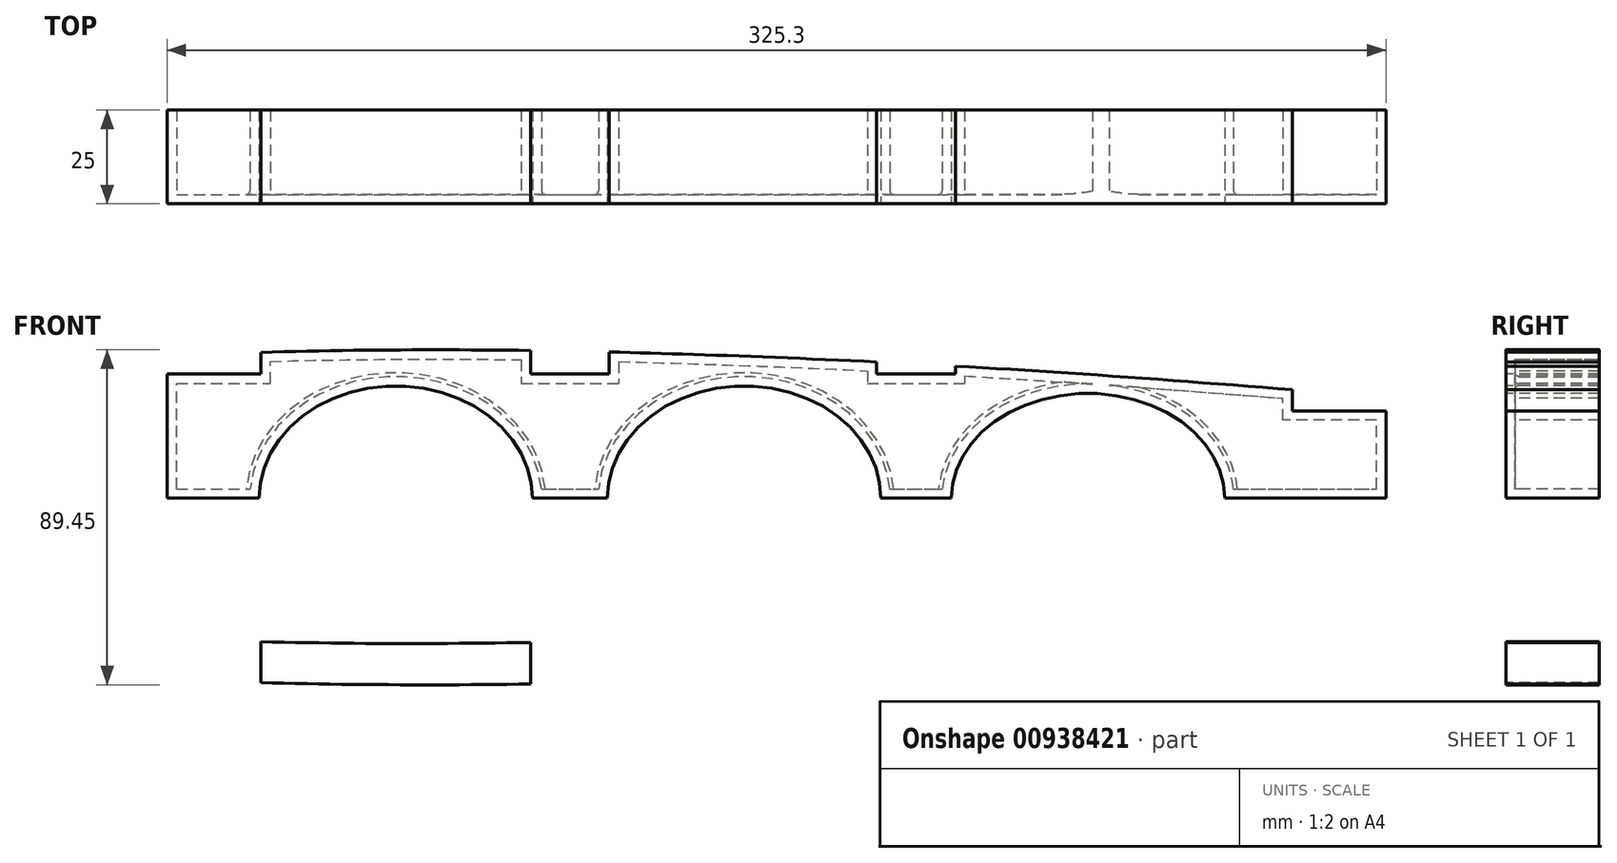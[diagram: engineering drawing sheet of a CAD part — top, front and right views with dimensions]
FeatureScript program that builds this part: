
annotation { "Feature Type Name" : "Feature", "Feature Type Description" : "" }
export const myFeature = defineFeature(function(context is Context, id is Id, definition is map)
    precondition{}
    {
        {
            var Q0;
            Q0=qCreatedBy(makeId("Front.planeOp"),FACE);
            var sketch = newSketch(context, id + "F0", { "sketchPlane" : qUnion([Q0])});
            skLineSegment(sketch, "E0", {"start": v(0, 0) * mm, "end": v(830, 0) * mm});
            skLineSegment(sketch, "E1", {"start": v(23.53, 0) * mm, "end": v(23.53, 22.98) * mm, "construction": true});
            skLineSegment(sketch, "E2", {"start": v(30.64, 0) * mm, "end": v(30.64, 25.86) * mm, "construction": true});
            skLineSegment(sketch, "E3", {"start": v(38.65, 0) * mm, "end": v(38.65, 28.62) * mm, "construction": true});
            skLineSegment(sketch, "E4", {"start": v(47.54, 0) * mm, "end": v(47.54, 31.24) * mm, "construction": true});
            skLineSegment(sketch, "E5", {"start": v(57.28, 0) * mm, "end": v(57.28, 33.72) * mm, "construction": true});
            skLineSegment(sketch, "E6", {"start": v(67.86, 0) * mm, "end": v(67.86, 36.05) * mm, "construction": true});
            skLineSegment(sketch, "E7", {"start": v(79.26, 0) * mm, "end": v(79.26, 38.22) * mm, "construction": true});
            skLineSegment(sketch, "E8", {"start": v(91.44, 0) * mm, "end": v(91.44, 40.22) * mm, "construction": true});
            skLineSegment(sketch, "E9", {"start": v(104.37, 0) * mm, "end": v(104.37, 42.04) * mm, "construction": true});
            skLineSegment(sketch, "E10", {"start": v(118.03, 0) * mm, "end": v(118.03, 43.68) * mm, "construction": true});
            skLineSegment(sketch, "E11", {"start": v(132.38, 0) * mm, "end": v(132.38, 45.13) * mm, "construction": true});
            skLineSegment(sketch, "E12", {"start": v(147.4, 0) * mm, "end": v(147.4, 46.38) * mm, "construction": true});
            skLineSegment(sketch, "E13", {"start": v(163.03, 0) * mm, "end": v(163.03, 47.45) * mm, "construction": true});
            skLineSegment(sketch, "E14", {"start": v(179.25, 0) * mm, "end": v(179.25, 48.31) * mm, "construction": true});
            skLineSegment(sketch, "E15", {"start": v(196.03, 0) * mm, "end": v(196.03, 48.98) * mm, "construction": true});
            skLineSegment(sketch, "E16", {"start": v(213.32, 0) * mm, "end": v(213.32, 49.45) * mm, "construction": true});
            skLineSegment(sketch, "E17", {"start": v(231.08, 0) * mm, "end": v(231.08, 49.73) * mm, "construction": true});
            skLineSegment(sketch, "E18", {"start": v(249.26, 0) * mm, "end": v(249.26, 49.81) * mm, "construction": true});
            skLineSegment(sketch, "E19", {"start": v(267.84, 0) * mm, "end": v(267.84, 49.72) * mm, "construction": true});
            skLineSegment(sketch, "E20", {"start": v(0.48, 0) * mm, "end": v(0.48, 3.54) * mm, "construction": true});
            skLineSegment(sketch, "E21", {"start": v(1.94, 0) * mm, "end": v(1.94, 7) * mm, "construction": true});
            skLineSegment(sketch, "E22", {"start": v(4.35, 0) * mm, "end": v(4.35, 10.38) * mm, "construction": true});
            skLineSegment(sketch, "E23", {"start": v(7.73, 0) * mm, "end": v(7.73, 13.67) * mm, "construction": true});
            skLineSegment(sketch, "E24", {"start": v(12.06, 0) * mm, "end": v(12.06, 16.87) * mm, "construction": true});
            skLineSegment(sketch, "E25", {"start": v(17.33, 0) * mm, "end": v(17.33, 19.98) * mm, "construction": true});
            skLineSegment(sketch, "E26", {"start": v(286.76, 0) * mm, "end": v(286.76, 49.45) * mm, "construction": true});
            skLineSegment(sketch, "E27", {"start": v(305.98, 0) * mm, "end": v(305.98, 49) * mm, "construction": true});
            skLineSegment(sketch, "E28", {"start": v(325.45, 0) * mm, "end": v(325.45, 48.4) * mm, "construction": true});
            skLineSegment(sketch, "E29", {"start": v(345.13, 0) * mm, "end": v(345.13, 47.64) * mm, "construction": true});
            skLineSegment(sketch, "E30", {"start": v(364.98, 0) * mm, "end": v(364.98, 46.75) * mm, "construction": true});
            skLineSegment(sketch, "E31", {"start": v(384.94, 0) * mm, "end": v(384.94, 45.71) * mm, "construction": true});
            skLineSegment(sketch, "E32", {"start": v(404.97, 0) * mm, "end": v(404.97, 44.56) * mm, "construction": true});
            skLineSegment(sketch, "E33", {"start": v(425.03, 0) * mm, "end": v(425.03, 43.3) * mm, "construction": true});
            skLineSegment(sketch, "E34", {"start": v(445.06, 0) * mm, "end": v(445.06, 41.93) * mm, "construction": true});
            skLineSegment(sketch, "E35", {"start": v(465.02, 0) * mm, "end": v(465.02, 40.47) * mm, "construction": true});
            skLineSegment(sketch, "E36", {"start": v(484.87, 0) * mm, "end": v(484.87, 38.94) * mm, "construction": true});
            skLineSegment(sketch, "E37", {"start": v(504.55, 0) * mm, "end": v(504.55, 37.33) * mm, "construction": true});
            skLineSegment(sketch, "E38", {"start": v(524.02, 0) * mm, "end": v(524.02, 35.67) * mm, "construction": true});
            skLineSegment(sketch, "E39", {"start": v(543.24, 0) * mm, "end": v(543.24, 33.96) * mm, "construction": true});
            skLineSegment(sketch, "E40", {"start": v(562.16, 0) * mm, "end": v(562.16, 32.21) * mm, "construction": true});
            skLineSegment(sketch, "E41", {"start": v(580.74, 0) * mm, "end": v(580.74, 30.44) * mm, "construction": true});
            skLineSegment(sketch, "E42", {"start": v(598.92, 0) * mm, "end": v(598.92, 28.64) * mm, "construction": true});
            skLineSegment(sketch, "E43", {"start": v(633.97, 0) * mm, "end": v(633.97, 25.03) * mm, "construction": true});
            skLineSegment(sketch, "E44", {"start": v(616.68, 0) * mm, "end": v(616.68, 26.83) * mm, "construction": true});
            skLineSegment(sketch, "E45", {"start": v(650.75, 0) * mm, "end": v(650.75, 23.23) * mm, "construction": true});
            skLineSegment(sketch, "E46", {"start": v(666.97, 0) * mm, "end": v(666.97, 21.44) * mm, "construction": true});
            skLineSegment(sketch, "E47", {"start": v(682.6, 0) * mm, "end": v(682.6, 19.68) * mm, "construction": true});
            skLineSegment(sketch, "E48", {"start": v(697.62, 0) * mm, "end": v(697.62, 17.96) * mm, "construction": true});
            skLineSegment(sketch, "E49", {"start": v(711.97, 0) * mm, "end": v(711.97, 16.27) * mm, "construction": true});
            skLineSegment(sketch, "E50", {"start": v(725.63, 0) * mm, "end": v(725.63, 14.64) * mm, "construction": true});
            skLineSegment(sketch, "E51", {"start": v(738.56, 0) * mm, "end": v(738.56, 13.06) * mm, "construction": true});
            skLineSegment(sketch, "E52", {"start": v(750.74, 0) * mm, "end": v(750.74, 11.55) * mm, "construction": true});
            skLineSegment(sketch, "E53", {"start": v(762.14, 0) * mm, "end": v(762.14, 10.11) * mm, "construction": true});
            skLineSegment(sketch, "E54", {"start": v(791.35, 0) * mm, "end": v(791.35, 6.32) * mm, "construction": true});
            skLineSegment(sketch, "E55", {"start": v(799.36, 0) * mm, "end": v(799.36, 5.25) * mm, "construction": true});
            skLineSegment(sketch, "E56", {"start": v(806.47, 0) * mm, "end": v(806.47, 4.29) * mm, "construction": true});
            skLineSegment(sketch, "E57", {"start": v(782.46, 0) * mm, "end": v(782.46, 7.49) * mm, "construction": true});
            skLineSegment(sketch, "E58", {"start": v(812.67, 0) * mm, "end": v(812.67, 3.45) * mm, "construction": true});
            skLineSegment(sketch, "E59", {"start": v(817.94, 0) * mm, "end": v(817.94, 2.72) * mm, "construction": true});
            skLineSegment(sketch, "E60", {"start": v(822.27, 0) * mm, "end": v(822.27, 2.12) * mm, "construction": true});
            skLineSegment(sketch, "E61", {"start": v(825.65, 0) * mm, "end": v(825.65, 1.65) * mm, "construction": true});
            skLineSegment(sketch, "E62", {"start": v(828.06, 0) * mm, "end": v(828.06, 1.32) * mm, "construction": true});
            skLineSegment(sketch, "E63", {"start": v(772.72, 0) * mm, "end": v(772.72, 8.76) * mm, "construction": true});
            skLineSegment(sketch, "E64", {"start": v(829.52, 0) * mm, "end": v(829.52, 1.11) * mm, "construction": true});
            skLineSegment(sketch, "E65", {"start": v(830, 0) * mm, "end": v(830, 1.05) * mm});
            skFitSpline(sketch, "E66", {"points": [v(0, 0) * mm, v(0.48, 3.54) * mm, v(1.94, 7) * mm, v(4.35, 10.38) * mm, v(7.73, 13.67) * mm, v(12.06, 16.87) * mm, v(17.33, 19.98) * mm, v(23.53, 22.98) * mm, v(30.64, 25.86) * mm, v(38.65, 28.62) * mm, v(47.54, 31.24) * mm, v(57.28, 33.72) * mm, v(67.86, 36.05) * mm, v(79.26, 38.22) * mm, v(91.44, 40.22) * mm, v(104.37, 42.04) * mm, v(118.03, 43.68) * mm, v(132.38, 45.13) * mm, v(147.4, 46.39) * mm, v(163.03, 47.45) * mm, v(179.25, 48.31) * mm, v(196.03, 48.98) * mm, v(213.32, 49.45) * mm, v(231.08, 49.73) * mm, v(249.26, 49.81) * mm, v(267.84, 49.72) * mm, v(286.76, 49.45) * mm, v(305.98, 49) * mm, v(325.45, 48.4) * mm, v(345.13, 47.64) * mm, v(364.98, 46.75) * mm, v(384.94, 45.71) * mm, v(404.97, 44.56) * mm, v(425.03, 43.3) * mm, v(445.06, 41.93) * mm, v(465.02, 40.47) * mm, v(484.87, 38.94) * mm, v(504.55, 37.33) * mm, v(524.02, 35.67) * mm, v(543.24, 33.96) * mm, v(562.16, 32.21) * mm, v(580.74, 30.44) * mm, v(598.92, 28.64) * mm, v(616.68, 26.83) * mm, v(633.97, 25.03) * mm, v(650.75, 23.23) * mm, v(666.97, 21.44) * mm, v(682.6, 19.68) * mm, v(697.62, 17.96) * mm, v(711.97, 16.27) * mm, v(725.63, 14.64) * mm, v(738.56, 13.06) * mm, v(750.74, 11.55) * mm, v(762.14, 10.11) * mm, v(772.72, 8.76) * mm, v(782.46, 7.49) * mm, v(791.35, 6.32) * mm, v(799.36, 5.25) * mm, v(806.47, 4.29) * mm, v(812.67, 3.45) * mm, v(817.94, 2.72) * mm, v(822.27, 2.12) * mm, v(825.65, 1.65) * mm, v(828.06, 1.32) * mm, v(829.52, 1.11) * mm, v(830, 1.05) * mm], "startDerivative": vector(34.1, 427.03) * mm, "endDerivative": vector(137.1, -19.25) * mm});
            skFitSpline(sketch, "E67.MirrorCS", {"points": [v(0, 0) * mm, v(0.48, -3.54) * mm, v(1.94, -7) * mm, v(4.35, -10.38) * mm, v(7.73, -13.67) * mm, v(12.06, -16.87) * mm, v(17.33, -19.98) * mm, v(23.53, -22.98) * mm, v(30.64, -25.86) * mm, v(38.65, -28.62) * mm, v(47.54, -31.24) * mm, v(57.28, -33.72) * mm, v(67.86, -36.05) * mm, v(79.26, -38.22) * mm, v(91.44, -40.22) * mm, v(104.37, -42.04) * mm, v(118.03, -43.68) * mm, v(132.38, -45.13) * mm, v(147.4, -46.39) * mm, v(163.03, -47.45) * mm, v(179.25, -48.31) * mm, v(196.03, -48.98) * mm, v(213.32, -49.45) * mm, v(231.08, -49.73) * mm, v(249.26, -49.81) * mm, v(267.84, -49.72) * mm, v(286.76, -49.45) * mm, v(305.98, -49) * mm, v(325.45, -48.4) * mm, v(345.13, -47.64) * mm, v(364.98, -46.75) * mm, v(384.94, -45.71) * mm, v(404.97, -44.56) * mm, v(425.03, -43.3) * mm, v(445.06, -41.93) * mm, v(465.02, -40.47) * mm, v(484.87, -38.94) * mm, v(504.55, -37.33) * mm, v(524.02, -35.67) * mm, v(543.24, -33.96) * mm, v(562.16, -32.21) * mm, v(580.74, -30.44) * mm, v(598.92, -28.64) * mm, v(616.68, -26.83) * mm, v(633.97, -25.03) * mm, v(650.75, -23.23) * mm, v(666.97, -21.44) * mm, v(682.6, -19.68) * mm, v(697.62, -17.96) * mm, v(711.97, -16.27) * mm, v(725.63, -14.64) * mm, v(738.56, -13.06) * mm, v(750.74, -11.55) * mm, v(762.14, -10.11) * mm, v(772.72, -8.76) * mm, v(782.46, -7.49) * mm, v(791.35, -6.32) * mm, v(799.36, -5.25) * mm, v(806.47, -4.29) * mm, v(812.67, -3.45) * mm, v(817.94, -2.72) * mm, v(822.27, -2.12) * mm, v(825.65, -1.65) * mm, v(828.06, -1.32) * mm, v(829.52, -1.11) * mm, v(830, -1.05) * mm], "startDerivative": vector(34.1, -427.03) * mm, "endDerivative": vector(137.1, 19.25) * mm});
            skLineSegment(sketch, "E68.MirrorCS", {"start": v(830, 0) * mm, "end": v(830, -1.05) * mm});
            skLineSegment(sketch, "E69", {"start": v(163.03, 47.45) * mm, "end": v(163.03, -47.45) * mm});
            skLineSegment(sketch, "E70", {"start": v(204.25, -49.23) * mm, "end": v(204.25, -33.23) * mm});
            skLineSegment(sketch, "E71", {"start": v(204.25, -33.23) * mm, "end": v(179.25, -33.23) * mm});
            skLineSegment(sketch, "E72", {"start": v(179.25, -33.23) * mm, "end": v(179.25, 33.23) * mm});
            skLineSegment(sketch, "E73", {"start": v(179.25, 33.23) * mm, "end": v(204.25, 33.23) * mm});
            skLineSegment(sketch, "E74", {"start": v(204.25, 33.23) * mm, "end": v(204.25, 49.23) * mm});
            skLineSegment(sketch, "E75", {"start": v(524.02, 35.67) * mm, "end": v(524.02, -35.67) * mm});
            skLineSegment(sketch, "E76", {"start": v(479.55, -39.36) * mm, "end": v(479.55, -23.36) * mm});
            skLineSegment(sketch, "E77", {"start": v(479.55, -23.36) * mm, "end": v(504.55, -23.36) * mm});
            skLineSegment(sketch, "E78", {"start": v(504.55, -23.36) * mm, "end": v(504.55, 23.36) * mm});
            skLineSegment(sketch, "E79", {"start": v(504.55, 23.36) * mm, "end": v(479.55, 23.36) * mm});
            skLineSegment(sketch, "E80", {"start": v(479.55, 23.36) * mm, "end": v(479.55, 39.36) * mm});
            skEllipse(sketch, "E81", {"center": v(240.25, 0) * mm, "majorRadius": 36.5 * mm, "minorRadius": 30 * mm, "majorAxis": v(1, 0)});
            skEllipse(sketch, "E82.1.0.0", {"center": v(333.25, 0) * mm, "majorRadius": 36.5 * mm, "minorRadius": 30 * mm, "majorAxis": v(1, 0)});
            skLineSegment(sketch, "E82.direction1", {"start": v(240.25, 0) * mm, "end": v(333.25, 0) * mm, "construction": true});
            skEllipse(sketch, "E83", {"center": v(425.03, 0) * mm, "majorRadius": 28 * mm, "minorRadius": 36.5 * mm, "majorAxis": v(0, -1)});
            skFitSpline(sketch, "E84.0", {"points": [v(19.9, 0) * mm, v(19.93, 0.28) * mm, v(19.97, 0.77) * mm, v(20.03, 1.33) * mm, v(20.07, 1.63) * mm, v(20.1, 1.78) * mm, v(20.12, 1.85) * mm, v(20.12, 1.88) * mm, v(20.13, 1.92) * mm, v(20.16, 1.99) * mm, v(20.2, 2.1) * mm, v(20.28, 2.3) * mm, v(20.43, 2.58) * mm, v(20.63, 2.94) * mm, v(20.87, 3.32) * mm, v(21.13, 3.7) * mm, v(21.53, 4.23) * mm, v(22.12, 4.91) * mm, v(22.98, 5.8) * mm, v(24.01, 6.71) * mm, v(25.19, 7.65) * mm, v(26.5, 8.6) * mm, v(28.4, 9.86) * mm, v(31.06, 11.42) * mm, v(34.64, 13.25) * mm, v(38.55, 15) * mm, v(44.15, 17.24) * mm, v(51.77, 19.86) * mm, v(61.74, 22.7) * mm, v(72.4, 25.26) * mm, v(83.62, 27.56) * mm, v(95.37, 29.62) * mm, v(107.56, 31.45) * mm, v(124.36, 33.6) * mm, v(146.26, 35.8) * mm, v(173.73, 37.69) * mm, v(202.17, 38.91) * mm, v(231.43, 39.53) * mm, v(261.35, 39.6) * mm, v(291.8, 39.18) * mm, v(322.69, 38.31) * mm, v(364.28, 36.62) * mm, v(416.8, 33.63) * mm, v(479.93, 28.95) * mm, v(531.98, 24.38) * mm, v(572.9, 20.44) * mm, v(603.14, 17.37) * mm, v(632.79, 14.2) * mm, v(661.73, 10.99) * mm, v(689.84, 7.73) * mm, v(716.93, 4.47) * mm, v(738.52, 1.78) * mm, v(755.07, -0.33) * mm, v(767.08, -1.9) * mm, v(778.65, -3.43) * mm, v(789.72, -4.91) * mm, v(800.24, -6.35) * mm, v(810.11, -7.7) * mm, v(817.7, -8.77) * mm, v(823.32, -9.57) * mm, v(826.6, -10.03) * mm, v(829.07, -10.39) * mm, v(830.84, -10.64) * mm, v(832.51, -10.88) * mm, v(834.08, -11.1) * mm, v(835.26, -11.27) * mm, v(836.14, -11.4) * mm, v(836.78, -11.5) * mm, v(837.37, -11.58) * mm, v(837.78, -11.64) * mm, v(838.05, -11.68) * mm, v(838.28, -11.71) * mm, v(838.4, -11.73) * mm, v(838.5, -11.74) * mm]});
            skFitSpline(sketch, "E85.MirrorCS", {"points": [v(19.9, 0) * mm, v(19.93, -0.28) * mm, v(19.97, -0.77) * mm, v(20.03, -1.33) * mm, v(20.08, -1.63) * mm, v(20.1, -1.78) * mm, v(20.12, -1.85) * mm, v(20.13, -1.87) * mm, v(20.14, -1.92) * mm, v(20.16, -1.99) * mm, v(20.2, -2.1) * mm, v(20.29, -2.29) * mm, v(20.44, -2.58) * mm, v(20.64, -2.94) * mm, v(20.88, -3.31) * mm, v(21.15, -3.7) * mm, v(21.55, -4.22) * mm, v(22.13, -4.9) * mm, v(23, -5.78) * mm, v(24.04, -6.7) * mm, v(25.22, -7.63) * mm, v(26.52, -8.57) * mm, v(28.44, -9.83) * mm, v(31.1, -11.38) * mm, v(34.7, -13.2) * mm, v(38.6, -14.93) * mm, v(44.21, -17.15) * mm, v(51.85, -19.74) * mm, v(61.83, -22.54) * mm, v(72.49, -25.06) * mm, v(83.73, -27.32) * mm, v(95.48, -29.34) * mm, v(107.68, -31.12) * mm, v(124.49, -33.22) * mm, v(146.4, -35.32) * mm, v(173.87, -37.11) * mm, v(202.32, -38.23) * mm, v(231.57, -38.74) * mm, v(261.5, -38.7) * mm, v(291.95, -38.16) * mm, v(322.83, -37.18) * mm, v(364.42, -35.33) * mm, v(416.93, -32.14) * mm, v(480.03, -27.22) * mm, v(532.07, -22.46) * mm, v(572.98, -18.36) * mm, v(603.2, -15.18) * mm, v(632.84, -11.91) * mm, v(661.77, -8.58) * mm, v(689.86, -5.22) * mm, v(716.95, -1.86) * mm, v(738.52, 0.91) * mm, v(755.06, 3.1) * mm, v(767.06, 4.7) * mm, v(778.63, 6.27) * mm, v(789.7, 7.8) * mm, v(800.21, 9.27) * mm, v(810.08, 10.67) * mm, v(817.67, 11.77) * mm, v(823.28, 12.58) * mm, v(826.56, 13.06) * mm, v(829.03, 13.42) * mm, v(830.8, 13.68) * mm, v(832.47, 13.93) * mm, v(834.03, 14.16) * mm, v(835.21, 14.33) * mm, v(836.1, 14.46) * mm, v(836.73, 14.56) * mm, v(837.32, 14.64) * mm, v(837.73, 14.7) * mm, v(838, 14.75) * mm, v(838.23, 14.78) * mm, v(838.36, 14.8) * mm, v(838.45, 14.81) * mm]});
            skLineSegment(sketch, "E86", {"start": v(100.03, 30.3) * mm, "end": v(134.03, 30.3) * mm});
            skLineSegment(sketch, "E87", {"start": v(140.03, 24.3) * mm, "end": v(140.03, -24.26) * mm});
            skLineSegment(sketch, "E88", {"start": v(133.98, -30.26) * mm, "end": v(100.03, -29.99) * mm});
            skPoint(sketch, "E89.visualSharp", {"position": v(140.03, 30.3) * mm});
            skArc(sketch, "E89.filletArc", {"start": v(140.03, 24.3) * mm, "mid": v(138.27, 28.55) * mm, "end": v(134.03, 30.3) * mm});
            skPoint(sketch, "E90.visualSharp", {"position": v(140.03, -30.3) * mm});
            skArc(sketch, "E90.filletArc", {"start": v(133.98, -30.26) * mm, "mid": v(138.25, -28.52) * mm, "end": v(140.03, -24.26) * mm});
            skEllipse(sketch, "E91", {"center": v(569.02, 0) * mm, "majorRadius": 20 * mm, "minorRadius": 22.5 * mm, "majorAxis": v(0, -1)});
            skLineSegment(sketch, "E92.bottom", {"start": v(625.97, -12) * mm, "end": v(665.97, -12) * mm});
            skLineSegment(sketch, "E92.top", {"start": v(625.97, 12) * mm, "end": v(665.97, 12) * mm});
            skLineSegment(sketch, "E92.left", {"start": v(623.97, -10) * mm, "end": v(623.97, 10) * mm});
            skLineSegment(sketch, "E92.right", {"start": v(665.97, -12) * mm, "end": v(665.97, 12) * mm});
            skPoint(sketch, "E92.middle", {"position": v(644.97, 0) * mm});
            skArc(sketch, "E93", {"start": v(665.97, 12) * mm, "mid": v(677.97, 0) * mm, "end": v(665.97, -12) * mm});
            skPoint(sketch, "E94.visualSharp", {"position": v(623.97, 12) * mm});
            skArc(sketch, "E94.filletArc", {"start": v(625.97, 12) * mm, "mid": v(624.56, 11.41) * mm, "end": v(623.97, 10) * mm});
            skPoint(sketch, "E95.visualSharp", {"position": v(623.97, -12) * mm});
            skArc(sketch, "E95.filletArc", {"start": v(623.97, -10) * mm, "mid": v(624.56, -11.41) * mm, "end": v(625.97, -12) * mm});
            skPoint(sketch, "E96", {"position": v(276.75, 0) * mm});
            skPoint(sketch, "E97", {"position": v(296.75, 0) * mm});
            skLineSegment(sketch, "E98.bottom", {"start": v(276.26, 65.67) * mm, "end": v(297.26, 65.67) * mm});
            skLineSegment(sketch, "E98.top", {"start": v(276.26, 33.23) * mm, "end": v(297.26, 33.23) * mm});
            skLineSegment(sketch, "E98.left", {"start": v(276.26, 65.67) * mm, "end": v(276.26, 33.23) * mm});
            skLineSegment(sketch, "E98.right", {"start": v(297.26, 65.67) * mm, "end": v(297.26, 33.23) * mm});
            skPoint(sketch, "E99", {"position": v(369.75, 0) * mm});
            skPoint(sketch, "E100", {"position": v(388.53, 0) * mm});
            skLineSegment(sketch, "E101", {"start": v(379.14, 0) * mm, "end": v(379.14, 46.03) * mm, "construction": true});
            skLineSegment(sketch, "E102.bottom", {"start": v(368.64, 58.81) * mm, "end": v(389.64, 58.81) * mm});
            skLineSegment(sketch, "E102.top", {"start": v(368.64, 33.23) * mm, "end": v(389.64, 33.23) * mm});
            skLineSegment(sketch, "E102.left", {"start": v(368.64, 58.81) * mm, "end": v(368.64, 33.23) * mm});
            skLineSegment(sketch, "E102.right", {"start": v(389.64, 58.81) * mm, "end": v(389.64, 33.23) * mm});
            skLineSegment(sketch, "E103.MirrorCS", {"start": v(297.26, -65.67) * mm, "end": v(297.26, -33.23) * mm});
            skLineSegment(sketch, "E104.MirrorCS", {"start": v(276.26, -65.67) * mm, "end": v(297.26, -65.67) * mm});
            skLineSegment(sketch, "E105.MirrorCS", {"start": v(276.26, -65.67) * mm, "end": v(276.26, -33.23) * mm});
            skLineSegment(sketch, "E106.MirrorCS", {"start": v(276.26, -33.23) * mm, "end": v(297.26, -33.23) * mm});
            skLineSegment(sketch, "E107.MirrorCS", {"start": v(368.64, -58.81) * mm, "end": v(389.64, -58.81) * mm});
            skLineSegment(sketch, "E108.MirrorCS", {"start": v(368.64, -58.81) * mm, "end": v(368.64, -33.23) * mm});
            skLineSegment(sketch, "E109.MirrorCS", {"start": v(389.64, -58.81) * mm, "end": v(389.64, -33.23) * mm});
            skLineSegment(sketch, "E110.MirrorCS", {"start": v(368.64, -33.23) * mm, "end": v(389.64, -33.23) * mm});
            skSolve(sketch);
        }
        {
            var Q0;
            {var subQ0=sQuery(id+"F0.wireOp",EDGE,"E73");Q0=makeQuery(id+"F0.imprint","IMPRINT",FACE,{"disambiguationData":[TD([[makeQuery(id+"F0.imprint","IMPRINT",EDGE,{"derivedFrom":subQ0}),-1.0]])]});}
            var Q1;
            {var subQ4=sQuery(id+"F0.wireOp",EDGE,"E70");Q1=makeQuery(id+"F0.imprint","IMPRINT",FACE,{"disambiguationData":[TD([[makeQuery(id+"F0.imprint","IMPRINT",EDGE,{"derivedFrom":subQ4}),-1.0]])]});}
            extrude(context, id + "F1", {"entities" : qUnion([Q0, Q1]), "oppositeDirection" : true, "depth" : 25 * mm, "offsetDistance" : 25 * mm});
        }
        {
            var Q0;
            Q0=makeQuery(id+"F1.opExtrude","CAP_FACE",FACE,{"disambiguationData":[OSD([sQuery(id+"F0.wireOp",EDGE,"E66"),sQuery(id+"F0.wireOp",EDGE,"E67.MirrorCS"),sQuery(id+"F0.wireOp",EDGE,"E70"),sQuery(id+"F0.wireOp",EDGE,"E71"),sQuery(id+"F0.wireOp",EDGE,"E72"),sQuery(id+"F0.wireOp",EDGE,"E73"),sQuery(id+"F0.wireOp",EDGE,"E74"),sQuery(id+"F0.wireOp",EDGE,"E76"),sQuery(id+"F0.wireOp",EDGE,"E77"),sQuery(id+"F0.wireOp",EDGE,"E78"),sQuery(id+"F0.wireOp",EDGE,"E79"),sQuery(id+"F0.wireOp",EDGE,"E80"),sQuery(id+"F0.wireOp",EDGE,"E81"),sQuery(id+"F0.wireOp",EDGE,"E82.1.0.0"),sQuery(id+"F0.wireOp",EDGE,"E83"),sQuery(id+"F0.wireOp",EDGE,"E98.top"),sQuery(id+"F0.wireOp",EDGE,"E98.left"),sQuery(id+"F0.wireOp",EDGE,"E98.right"),sQuery(id+"F0.wireOp",EDGE,"E102.top"),sQuery(id+"F0.wireOp",EDGE,"E102.left"),sQuery(id+"F0.wireOp",EDGE,"E102.right"),sQuery(id+"F0.wireOp",EDGE,"E103.MirrorCS"),sQuery(id+"F0.wireOp",EDGE,"E105.MirrorCS"),sQuery(id+"F0.wireOp",EDGE,"E106.MirrorCS"),sQuery(id+"F0.wireOp",EDGE,"E108.MirrorCS"),sQuery(id+"F0.wireOp",EDGE,"E109.MirrorCS"),sQuery(id+"F0.wireOp",EDGE,"E110.MirrorCS")])],"isStart":false});
            shell(context, id + "F2", {"entities" : qUnion([Q0]), "thickness" : 2.5 * mm});
        }
        {
            var Q0;
            {var subQ0=sQuery(id+"F0.wireOp",EDGE,"E83");Q0=makeQuery(id+"F2.opShell","OFFSET_EDGE",EDGE,{"disambiguationData":[OSD([subQ0]),TDD([makeQuery(id+"F1.opExtrude","CAP_EDGE",EDGE,{"disambiguationData":[OSD([subQ0])],"isStart":true})])]});}
            var Q1;
            {var subQ0=sQuery(id+"F0.wireOp",EDGE,"E82.1.0.0");Q1=makeQuery(id+"F2.opShell","OFFSET_EDGE",EDGE,{"disambiguationData":[OSD([subQ0]),TDD([makeQuery(id+"F1.opExtrude","CAP_EDGE",EDGE,{"disambiguationData":[OSD([subQ0])],"isStart":true})])]});}
            var Q2;
            {var subQ0=sQuery(id+"F0.wireOp",EDGE,"E81");Q2=makeQuery(id+"F2.opShell","OFFSET_EDGE",EDGE,{"disambiguationData":[OSD([subQ0]),TDD([makeQuery(id+"F1.opExtrude","CAP_EDGE",EDGE,{"disambiguationData":[OSD([subQ0])],"isStart":true})])]});}
            fillet(context, id + "F3", {"entities" : qUnion([Q0, Q1, Q2]), "radius" : 1 * mm, "tangentPropagation" : true, "allowEdgeOverflow" : false});
        }
    });
